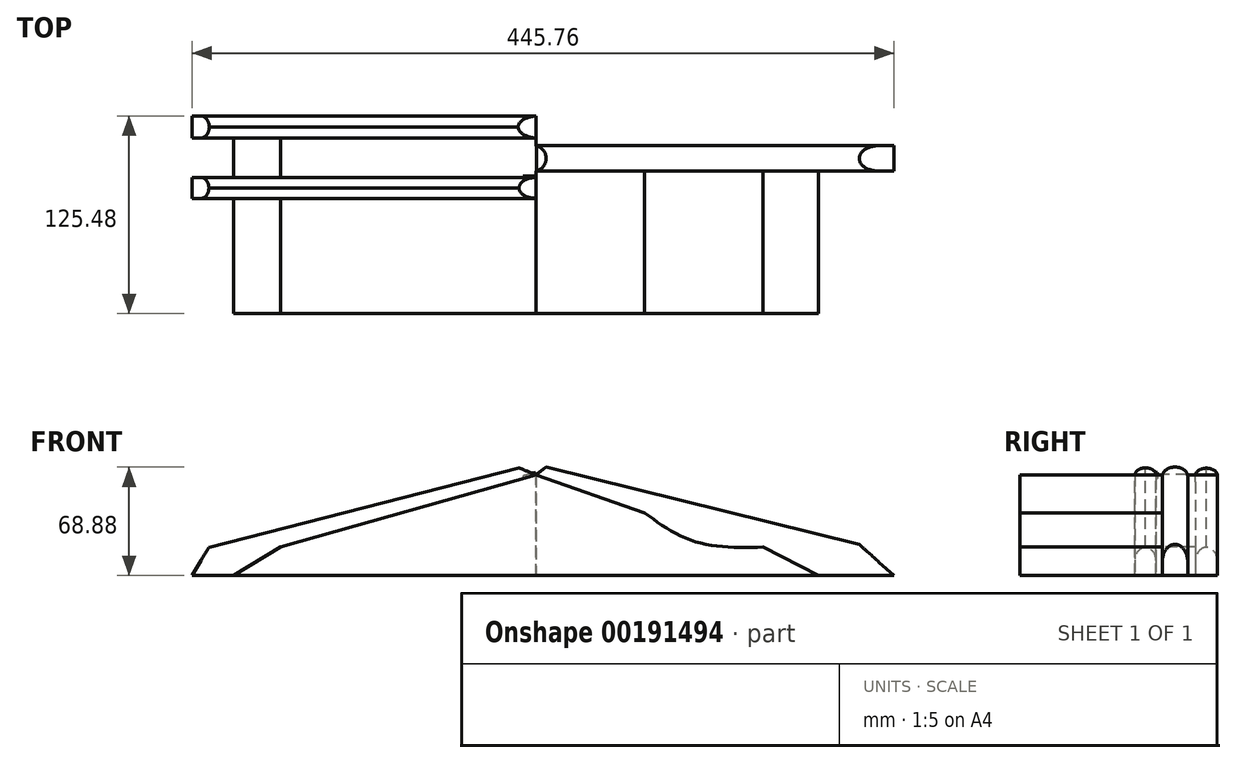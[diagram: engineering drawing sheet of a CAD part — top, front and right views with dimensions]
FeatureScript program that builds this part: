
annotation { "Feature Type Name" : "Feature", "Feature Type Description" : "" }
export const myFeature = defineFeature(function(context is Context, id is Id, definition is map)
    precondition{}
    {
        {
            var Q0;
            Q0=qCreatedBy(makeId("Front.planeOp"),FACE);
            var sketch = newSketch(context, id + "F0", { "sketchPlane" : qUnion([Q0])});
            skLineSegment(sketch, "E0", {"start": v(236.53, -70.44) * mm, "end": v(201.58, -52.42) * mm});
            skFitSpline(sketch, "E1", {"points": [v(201.58, -52.42) * mm, v(158.91, -49.1) * mm, v(126.17, -30.72) * mm], "startDerivative": vector(-86.5, -1.75) * mm, "endDerivative": vector(-64.07, 45.67) * mm});
            skLineSegment(sketch, "E2", {"start": v(126.17, -30.72) * mm, "end": v(57.38, -6.44) * mm});
            skLineSegment(sketch, "E3", {"start": v(57.38, -6.44) * mm, "end": v(-104.84, -52.42) * mm});
            skLineSegment(sketch, "E4", {"start": v(-104.84, -52.42) * mm, "end": v(-134.63, -70.44) * mm});
            skLineSegment(sketch, "E5", {"start": v(-134.63, -70.44) * mm, "end": v(236.53, -70.44) * mm});
            skSolve(sketch);
        }
        {
            var Q0;
            Q0 = qSketchRegion(id + "F0", true);
            extrude(context, id + "F1", {"entities" : qUnion([Q0]), "oppositeDirection" : true, "depth" : 68.83 * mm});
        }
        {
            var Q0;
            Q0=makeQuery(id+"F1.opExtrude","CAP_FACE",FACE,{"disambiguationData":[OSD([sQuery(id+"F0.wireOp",EDGE,"E0"),sQuery(id+"F0.wireOp",EDGE,"E1"),sQuery(id+"F0.wireOp",EDGE,"E2"),sQuery(id+"F0.wireOp",EDGE,"E3"),sQuery(id+"F0.wireOp",EDGE,"E4"),sQuery(id+"F0.wireOp",EDGE,"E5")])],"isStart":false});
            var sketch = newSketch(context, id + "F2", { "sketchPlane" : qUnion([Q0])});
            skLineSegment(sketch, "E6", {"start": v(-57.38, -6.44) * mm, "end": v(-57.38, -70.44) * mm});
            skLineSegment(sketch, "E7", {"start": v(-57.38, -70.44) * mm, "end": v(134.63, -70.44) * mm});
            skLineSegment(sketch, "E8", {"start": v(134.63, -70.44) * mm, "end": v(104.84, -52.42) * mm});
            skLineSegment(sketch, "E9", {"start": v(104.84, -52.42) * mm, "end": v(-57.38, -6.44) * mm});
            skSolve(sketch);
        }
        {
            var Q0;
            Q0 = qSketchRegion(id + "F2", true);
            extrude(context, id + "F3", {"entities" : qUnion([Q0]), "operationType" : NewBodyOperationType.ADD, "depth" : 56.64 * mm});
        }
        {
            var Q0;
            Q0=makeQuery(id+"F1.opExtrude","CAP_FACE",FACE,{"disambiguationData":[OSD([sQuery(id+"F0.wireOp",EDGE,"E0"),sQuery(id+"F0.wireOp",EDGE,"E1"),sQuery(id+"F0.wireOp",EDGE,"E2"),sQuery(id+"F0.wireOp",EDGE,"E3"),sQuery(id+"F0.wireOp",EDGE,"E4"),sQuery(id+"F0.wireOp",EDGE,"E5")])],"isStart":false});
            extrude(context, id + "F4", {"entities" : qUnion([Q0]), "operationType" : NewBodyOperationType.ADD, "depth" : 21.59 * mm});
        }
        {
            var Q0;
            Q0=makeQuery(id+"F4.opExtrude","CAP_FACE",FACE,{"disambiguationData":[OSD([sQuery(id+"F0.wireOp",EDGE,"E0"),sQuery(id+"F0.wireOp",EDGE,"E1"),sQuery(id+"F0.wireOp",EDGE,"E2"),sQuery(id+"F0.wireOp",EDGE,"E3"),sQuery(id+"F0.wireOp",EDGE,"E4"),sQuery(id+"F0.wireOp",EDGE,"E5")])],"isStart":false});
            var sketch = newSketch(context, id + "F5", { "sketchPlane" : qUnion([Q0])});
            skLineSegment(sketch, "E10", {"start": v(-284.8, -70.44) * mm, "end": v(-57.38, -70.44) * mm});
            skLineSegment(sketch, "E11", {"start": v(-57.38, -70.44) * mm, "end": v(-57.38, 0) * mm});
            skLineSegment(sketch, "E12", {"start": v(-57.38, 0) * mm, "end": v(-284.8, -56.17) * mm});
            skLineSegment(sketch, "E13", {"start": v(-284.8, -56.17) * mm, "end": v(-284.8, -70.44) * mm});
            skSolve(sketch);
        }
        {
            var Q0;
            Q0 = qSketchRegion(id + "F5", true);
            extrude(context, id + "F6", {"entities" : qUnion([Q0]), "operationType" : NewBodyOperationType.ADD, "depth" : 16.26 * mm});
        }
        {
            var Q0;
            Q0=makeQuery(id+"F6.opExtrude","SWEPT_EDGE",EDGE,{"disambiguationData":[OSD([sQuery(id+"F5.wireOp",EDGE,"E12"),sQuery(id+"F5.wireOp",EDGE,"E13")])]});
            chamfer(context, id + "F7", {"entities" : qUnion([Q0]), "chamferType" : ChamferType.TWO_OFFSETS, "width1" : 22.86 * mm, "oppositeDirection" : true, "width2" : 14.48 * mm, "tangentPropagation" : true});
        }
        {
            var Q0;
            Q0=makeQuery(id+"F6.opExtrude","SWEPT_EDGE",EDGE,{"disambiguationData":[OSD([sQuery(id+"F5.wireOp",EDGE,"E11"),sQuery(id+"F5.wireOp",EDGE,"E12")])]});
            chamfer(context, id + "F8", {"entities" : qUnion([Q0]), "width" : 5.08 * mm, "tangentPropagation" : true});
        }
        {
            var Q0;
            Q0=makeQuery(id+"F6.opExtrude","CAP_EDGE",EDGE,{"disambiguationData":[OSD([sQuery(id+"F5.wireOp",EDGE,"E12")])],"isStart":false});
            var Q1;
            Q1=makeQuery(id+"F6.opExtrude","CAP_EDGE",EDGE,{"disambiguationData":[OSD([sQuery(id+"F5.wireOp",EDGE,"E12")])],"isStart":true});
            fillet(context, id + "F9", {"entities" : qUnion([Q0, Q1]), "radius" : 7.97 * mm, "tangentPropagation" : true, "allowEdgeOverflow" : false});
        }
        {
            var Q0;
            Q0=makeQuery(id+"F3.opExtrude","CAP_FACE",FACE,{"disambiguationData":[OSD([sQuery(id+"F2.wireOp",EDGE,"E6"),sQuery(id+"F2.wireOp",EDGE,"E7"),sQuery(id+"F2.wireOp",EDGE,"E8"),sQuery(id+"F2.wireOp",EDGE,"E9")])],"isStart":false});
            var sketch = newSketch(context, id + "F10", { "sketchPlane" : qUnion([Q0])});
            skLineSegment(sketch, "E14", {"start": v(-57.38, -6.44) * mm, "end": v(-45.83, -2.23) * mm});
            skLineSegment(sketch, "E15", {"start": v(-45.83, -2.23) * mm, "end": v(150.17, -52.42) * mm});
            skLineSegment(sketch, "E16", {"start": v(150.17, -52.42) * mm, "end": v(161.17, -70.44) * mm});
            skLineSegment(sketch, "E17", {"start": v(161.17, -70.44) * mm, "end": v(134.63, -70.44) * mm});
            skLineSegment(sketch, "E18", {"start": v(134.63, -70.44) * mm, "end": v(104.84, -52.42) * mm});
            skLineSegment(sketch, "E19", {"start": v(104.84, -52.42) * mm, "end": v(-57.38, -6.44) * mm});
            skSolve(sketch);
        }
        {
            var Q0;
            Q0 = qSketchRegion(id + "F10", true);
            extrude(context, id + "F11", {"entities" : qUnion([Q0]), "operationType" : NewBodyOperationType.ADD, "oppositeDirection" : true, "depth" : 13.97 * mm});
        }
        {
            var Q0;
            Q0=makeQuery(id+"F11.opExtrude","CAP_EDGE",EDGE,{"disambiguationData":[OSD([sQuery(id+"F10.wireOp",EDGE,"E15")])],"isStart":true});
            var Q1;
            Q1=makeQuery(id+"F11.opExtrude","CAP_EDGE",EDGE,{"disambiguationData":[OSD([sQuery(id+"F10.wireOp",EDGE,"E15")])],"isStart":false});
            fillet(context, id + "F12", {"entities" : qUnion([Q0, Q1]), "radius" : 7.36 * mm, "tangentPropagation" : true, "allowEdgeOverflow" : false});
        }
        {
            var Q0;
            Q0=makeQuery(id+"F3.boolean.opBoolean","MERGE",FACE,{"derivedFrom":[makeQuery(id+"F1.opExtrude","SWEPT_FACE",FACE,{"disambiguationData":[OSD([sQuery(id+"F0.wireOp",EDGE,"E3")])]}),makeQuery(id+"F3.opExtrude","SWEPT_FACE",FACE,{"disambiguationData":[OSD([sQuery(id+"F2.wireOp",EDGE,"E9")])]})]});
            var sketch = newSketch(context, id + "F13", { "sketchPlane" : qUnion([Q0])});
            skLineSegment(sketch, "E20.bottom", {"start": v(53.45, 86.4) * mm, "end": v(45.21, 86.4) * mm});
            skLineSegment(sketch, "E20.top", {"start": v(53.45, 87.5) * mm, "end": v(45.21, 87.5) * mm});
            skLineSegment(sketch, "E20.left", {"start": v(53.45, 86.4) * mm, "end": v(53.45, 87.5) * mm});
            skLineSegment(sketch, "E20.right", {"start": v(45.21, 86.4) * mm, "end": v(45.21, 87.5) * mm});
            skSolve(sketch);
        }
        {
            var Q0;
            Q0 = qSketchRegion(id + "F13", true);
            extrude(context, id + "F14", {"entities" : qUnion([Q0]), "operationType" : NewBodyOperationType.ADD, "depth" : 1.52 * mm});
        }
        {
            var Q0;
            Q0=makeQuery(id+"F14.opExtrude","SWEPT_FACE",FACE,{"disambiguationData":[OSD([sQuery(id+"F13.wireOp",EDGE,"E20.bottom")])]});
            var sketch = newSketch(context, id + "F15", { "sketchPlane" : qUnion([Q0])});
            skLineSegment(sketch, "E21", {"start": v(57.38, -6.44) * mm, "end": v(46.46, -2.06) * mm});
            skLineSegment(sketch, "E22", {"start": v(46.46, -2.06) * mm, "end": v(-150.44, -52.48) * mm});
            skLineSegment(sketch, "E23", {"start": v(-150.44, -52.48) * mm, "end": v(-161.18, -70.37) * mm});
            skLineSegment(sketch, "E24", {"start": v(-161.18, -70.37) * mm, "end": v(-134.12, -70.37) * mm});
            skLineSegment(sketch, "E25", {"start": v(-134.12, -70.37) * mm, "end": v(-104.82, -52.48) * mm});
            skLineSegment(sketch, "E26", {"start": v(-104.82, -52.48) * mm, "end": v(57.38, -6.44) * mm});
            skSolve(sketch);
        }
        {
            var Q0;
            Q0 = qSketchRegion(id + "F15", true);
            extrude(context, id + "F16", {"entities" : qUnion([Q0]), "operationType" : NewBodyOperationType.ADD, "depth" : 13.2 * mm});
        }
        {
            var Q0;
            Q0=makeQuery(id+"F16.opExtrude","CAP_EDGE",EDGE,{"disambiguationData":[OSD([sQuery(id+"F15.wireOp",EDGE,"E22")])],"isStart":false});
            var Q1;
            Q1=makeQuery(id+"F16.opExtrude","CAP_EDGE",EDGE,{"disambiguationData":[OSD([sQuery(id+"F15.wireOp",EDGE,"E22")])],"isStart":true});
            fillet(context, id + "F17", {"entities" : qUnion([Q0, Q1]), "radius" : 6.75 * mm, "tangentPropagation" : true, "allowEdgeOverflow" : false});
        }
    });
